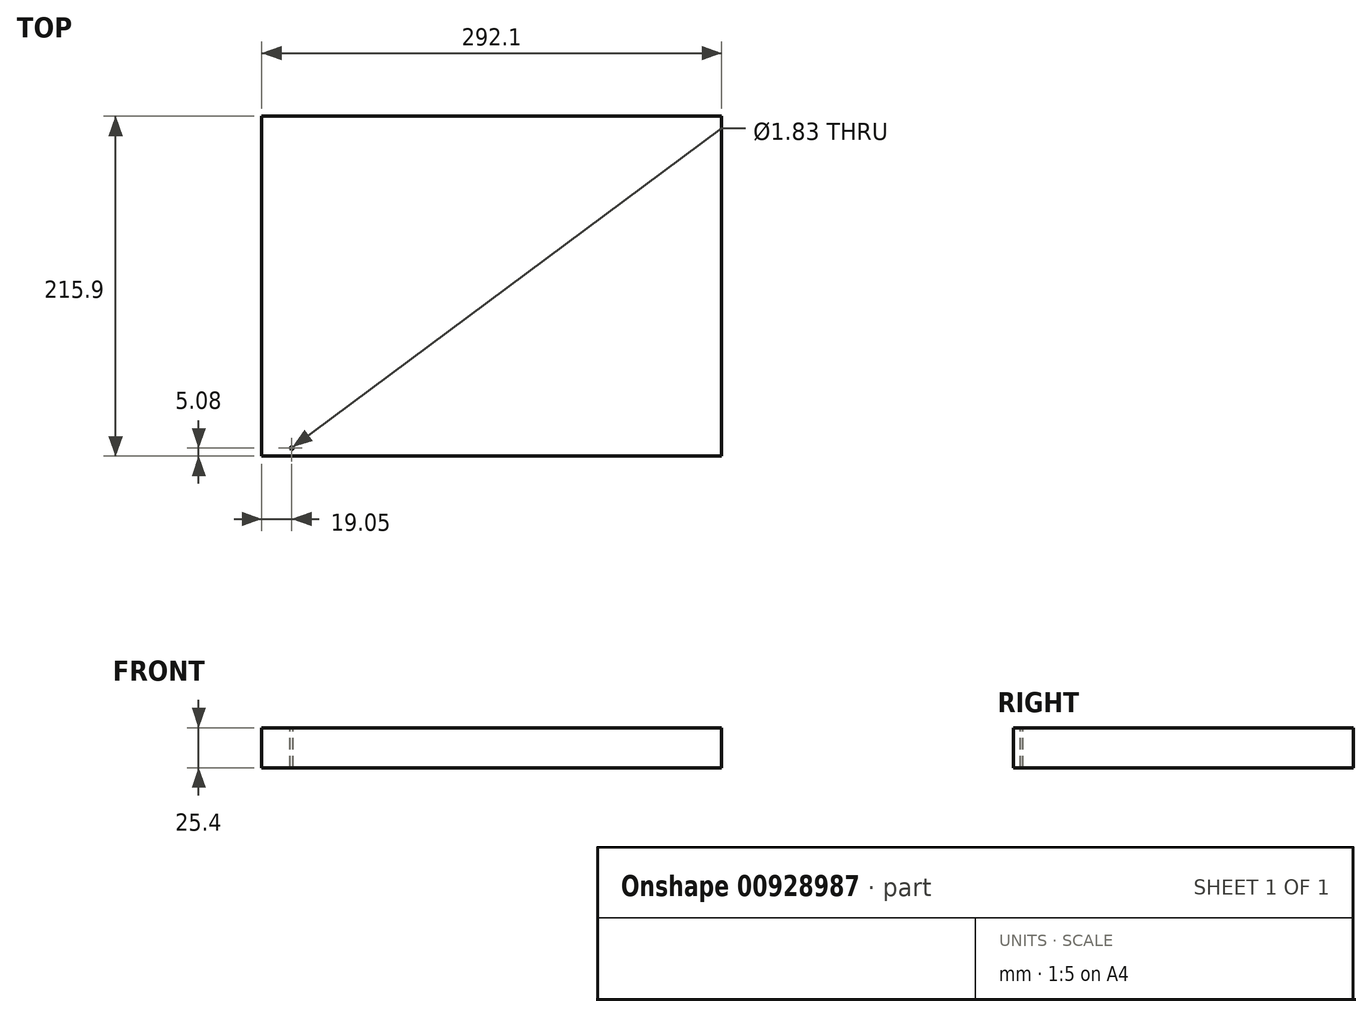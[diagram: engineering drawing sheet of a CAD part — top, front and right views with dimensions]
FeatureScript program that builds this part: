
annotation { "Feature Type Name" : "Feature", "Feature Type Description" : "" }
export const myFeature = defineFeature(function(context is Context, id is Id, definition is map)
    precondition{}
    {
        {
            var Q0;
            Q0=qCreatedBy(makeId("Top.planeOp"),FACE);
            var sketch = newSketch(context, id + "F0", { "sketchPlane" : qUnion([Q0])});
            skLineSegment(sketch, "E0.bottom", {"start": v(146.05, 107.95) * mm, "end": v(-146.05, 107.95) * mm});
            skLineSegment(sketch, "E0.top", {"start": v(146.05, -107.95) * mm, "end": v(-146.05, -107.95) * mm});
            skLineSegment(sketch, "E0.left", {"start": v(146.05, 107.95) * mm, "end": v(146.05, -107.95) * mm});
            skLineSegment(sketch, "E0.right", {"start": v(-146.05, 107.95) * mm, "end": v(-146.05, -107.95) * mm});
            skPoint(sketch, "E0.middle", {"position": v(0, 0) * mm});
            skSolve(sketch);
        }
        {
            var Q0;
            Q0=makeQuery(id+"F0.imprint","IMPRINT",FACE,{"disambiguationData":[TD([[makeQuery(id+"F0.imprint","IMPRINT",EDGE,{"derivedFrom":sQuery(id+"F0.wireOp",EDGE,"E0.bottom")}),1.0]])]});
            extrude(context, id + "F1", {"entities" : qUnion([Q0]), "depth" : 25.4 * mm, "offsetDistance" : 25.4 * mm});
        }
        {
            var Q0;
            Q0=makeQuery(id+"F1.opExtrude","CAP_FACE",FACE,{"disambiguationData":[OSD([sQuery(id+"F0.wireOp",EDGE,"E0.bottom"),sQuery(id+"F0.wireOp",EDGE,"E0.top"),sQuery(id+"F0.wireOp",EDGE,"E0.left"),sQuery(id+"F0.wireOp",EDGE,"E0.right")])],"isStart":false});
            var sketch = newSketch(context, id + "F2", { "sketchPlane" : qUnion([Q0])});
            skCircle(sketch, "E1", {"center": v(-127, -102.87) * mm, "radius": 0.91 * mm});
            skCircle(sketch, "E2.1.0.0", {"center": v(-124.46, -102.87) * mm, "radius": 0.91 * mm});
            skCircle(sketch, "E2.2.0.0", {"center": v(-121.92, -102.87) * mm, "radius": 0.91 * mm});
            skCircle(sketch, "E2.3.0.0", {"center": v(-119.38, -102.87) * mm, "radius": 0.91 * mm});
            skCircle(sketch, "E2.4.0.0", {"center": v(-116.84, -102.87) * mm, "radius": 0.91 * mm});
            skCircle(sketch, "E2.5.0.0", {"center": v(-114.3, -102.87) * mm, "radius": 0.91 * mm});
            skCircle(sketch, "E2.6.0.0", {"center": v(-111.76, -102.87) * mm, "radius": 0.91 * mm});
            skCircle(sketch, "E2.7.0.0", {"center": v(-109.22, -102.87) * mm, "radius": 0.91 * mm});
            skCircle(sketch, "E2.8.0.0", {"center": v(-106.68, -102.87) * mm, "radius": 0.91 * mm});
            skCircle(sketch, "E2.9.0.0", {"center": v(-104.14, -102.87) * mm, "radius": 0.91 * mm});
            skCircle(sketch, "E2.10.0.0", {"center": v(-101.6, -102.87) * mm, "radius": 0.91 * mm});
            skCircle(sketch, "E2.11.0.0", {"center": v(-99.06, -102.87) * mm, "radius": 0.91 * mm});
            skCircle(sketch, "E2.12.0.0", {"center": v(-96.52, -102.87) * mm, "radius": 0.91 * mm});
            skCircle(sketch, "E2.13.0.0", {"center": v(-93.98, -102.87) * mm, "radius": 0.91 * mm});
            skCircle(sketch, "E2.14.0.0", {"center": v(-91.44, -102.87) * mm, "radius": 0.91 * mm});
            skCircle(sketch, "E2.15.0.0", {"center": v(-88.9, -102.87) * mm, "radius": 0.91 * mm});
            skCircle(sketch, "E2.16.0.0", {"center": v(-86.36, -102.87) * mm, "radius": 0.91 * mm});
            skCircle(sketch, "E2.17.0.0", {"center": v(-83.82, -102.87) * mm, "radius": 0.91 * mm});
            skCircle(sketch, "E2.18.0.0", {"center": v(-81.28, -102.87) * mm, "radius": 0.91 * mm});
            skCircle(sketch, "E2.19.0.0", {"center": v(-78.74, -102.87) * mm, "radius": 0.91 * mm});
            skCircle(sketch, "E2.20.0.0", {"center": v(-76.2, -102.87) * mm, "radius": 0.91 * mm});
            skCircle(sketch, "E2.21.0.0", {"center": v(-73.66, -102.87) * mm, "radius": 0.91 * mm});
            skCircle(sketch, "E2.22.0.0", {"center": v(-71.12, -102.87) * mm, "radius": 0.91 * mm});
            skCircle(sketch, "E2.23.0.0", {"center": v(-68.58, -102.87) * mm, "radius": 0.91 * mm});
            skCircle(sketch, "E2.24.0.0", {"center": v(-66.04, -102.87) * mm, "radius": 0.91 * mm});
            skCircle(sketch, "E2.25.0.0", {"center": v(-63.5, -102.87) * mm, "radius": 0.91 * mm});
            skCircle(sketch, "E2.26.0.0", {"center": v(-60.96, -102.87) * mm, "radius": 0.91 * mm});
            skCircle(sketch, "E2.27.0.0", {"center": v(-58.42, -102.87) * mm, "radius": 0.91 * mm});
            skCircle(sketch, "E2.28.0.0", {"center": v(-55.88, -102.87) * mm, "radius": 0.91 * mm});
            skCircle(sketch, "E2.29.0.0", {"center": v(-53.34, -102.87) * mm, "radius": 0.91 * mm});
            skCircle(sketch, "E2.30.0.0", {"center": v(-50.8, -102.87) * mm, "radius": 0.91 * mm});
            skCircle(sketch, "E2.31.0.0", {"center": v(-48.26, -102.87) * mm, "radius": 0.91 * mm});
            skCircle(sketch, "E2.32.0.0", {"center": v(-45.72, -102.87) * mm, "radius": 0.91 * mm});
            skCircle(sketch, "E2.33.0.0", {"center": v(-43.18, -102.87) * mm, "radius": 0.91 * mm});
            skCircle(sketch, "E2.34.0.0", {"center": v(-40.64, -102.87) * mm, "radius": 0.91 * mm});
            skCircle(sketch, "E2.35.0.0", {"center": v(-38.1, -102.87) * mm, "radius": 0.91 * mm});
            skCircle(sketch, "E2.36.0.0", {"center": v(-35.56, -102.87) * mm, "radius": 0.91 * mm});
            skCircle(sketch, "E2.37.0.0", {"center": v(-33.02, -102.87) * mm, "radius": 0.91 * mm});
            skCircle(sketch, "E2.38.0.0", {"center": v(-30.48, -102.87) * mm, "radius": 0.91 * mm});
            skCircle(sketch, "E2.39.0.0", {"center": v(-27.94, -102.87) * mm, "radius": 0.91 * mm});
            skCircle(sketch, "E2.40.0.0", {"center": v(-25.4, -102.87) * mm, "radius": 0.91 * mm});
            skCircle(sketch, "E2.41.0.0", {"center": v(-22.86, -102.87) * mm, "radius": 0.91 * mm});
            skCircle(sketch, "E2.42.0.0", {"center": v(-20.32, -102.87) * mm, "radius": 0.91 * mm});
            skCircle(sketch, "E2.43.0.0", {"center": v(-17.78, -102.87) * mm, "radius": 0.91 * mm});
            skCircle(sketch, "E2.44.0.0", {"center": v(-15.24, -102.87) * mm, "radius": 0.91 * mm});
            skCircle(sketch, "E2.45.0.0", {"center": v(-12.7, -102.87) * mm, "radius": 0.91 * mm});
            skCircle(sketch, "E2.46.0.0", {"center": v(-10.16, -102.87) * mm, "radius": 0.91 * mm});
            skCircle(sketch, "E2.47.0.0", {"center": v(-7.62, -102.87) * mm, "radius": 0.91 * mm});
            skCircle(sketch, "E2.48.0.0", {"center": v(-5.08, -102.87) * mm, "radius": 0.91 * mm});
            skCircle(sketch, "E2.49.0.0", {"center": v(-2.54, -102.87) * mm, "radius": 0.91 * mm});
            skCircle(sketch, "E2.50.0.0", {"center": v(0, -102.87) * mm, "radius": 0.91 * mm});
            skCircle(sketch, "E2.51.0.0", {"center": v(2.54, -102.87) * mm, "radius": 0.91 * mm});
            skCircle(sketch, "E2.52.0.0", {"center": v(5.08, -102.87) * mm, "radius": 0.91 * mm});
            skCircle(sketch, "E2.53.0.0", {"center": v(7.62, -102.87) * mm, "radius": 0.91 * mm});
            skCircle(sketch, "E2.54.0.0", {"center": v(10.16, -102.87) * mm, "radius": 0.91 * mm});
            skCircle(sketch, "E2.55.0.0", {"center": v(12.7, -102.87) * mm, "radius": 0.91 * mm});
            skCircle(sketch, "E2.56.0.0", {"center": v(15.24, -102.87) * mm, "radius": 0.91 * mm});
            skCircle(sketch, "E2.57.0.0", {"center": v(17.78, -102.87) * mm, "radius": 0.91 * mm});
            skCircle(sketch, "E2.58.0.0", {"center": v(20.32, -102.87) * mm, "radius": 0.91 * mm});
            skCircle(sketch, "E2.59.0.0", {"center": v(22.86, -102.87) * mm, "radius": 0.91 * mm});
            skCircle(sketch, "E2.60.0.0", {"center": v(25.4, -102.87) * mm, "radius": 0.91 * mm});
            skCircle(sketch, "E2.61.0.0", {"center": v(27.94, -102.87) * mm, "radius": 0.91 * mm});
            skCircle(sketch, "E2.62.0.0", {"center": v(30.48, -102.87) * mm, "radius": 0.91 * mm});
            skCircle(sketch, "E2.63.0.0", {"center": v(33.02, -102.87) * mm, "radius": 0.91 * mm});
            skCircle(sketch, "E2.64.0.0", {"center": v(35.56, -102.87) * mm, "radius": 0.91 * mm});
            skCircle(sketch, "E2.65.0.0", {"center": v(38.1, -102.87) * mm, "radius": 0.91 * mm});
            skCircle(sketch, "E2.66.0.0", {"center": v(40.64, -102.87) * mm, "radius": 0.91 * mm});
            skCircle(sketch, "E2.67.0.0", {"center": v(43.18, -102.87) * mm, "radius": 0.91 * mm});
            skCircle(sketch, "E2.68.0.0", {"center": v(45.72, -102.87) * mm, "radius": 0.91 * mm});
            skCircle(sketch, "E2.69.0.0", {"center": v(48.26, -102.87) * mm, "radius": 0.91 * mm});
            skCircle(sketch, "E2.70.0.0", {"center": v(50.8, -102.87) * mm, "radius": 0.91 * mm});
            skCircle(sketch, "E2.71.0.0", {"center": v(53.34, -102.87) * mm, "radius": 0.91 * mm});
            skCircle(sketch, "E2.72.0.0", {"center": v(55.88, -102.87) * mm, "radius": 0.91 * mm});
            skCircle(sketch, "E2.73.0.0", {"center": v(58.42, -102.87) * mm, "radius": 0.91 * mm});
            skCircle(sketch, "E2.74.0.0", {"center": v(60.96, -102.87) * mm, "radius": 0.91 * mm});
            skCircle(sketch, "E2.75.0.0", {"center": v(63.5, -102.87) * mm, "radius": 0.91 * mm});
            skCircle(sketch, "E2.76.0.0", {"center": v(66.04, -102.87) * mm, "radius": 0.91 * mm});
            skCircle(sketch, "E2.77.0.0", {"center": v(68.58, -102.87) * mm, "radius": 0.91 * mm});
            skCircle(sketch, "E2.78.0.0", {"center": v(71.12, -102.87) * mm, "radius": 0.91 * mm});
            skCircle(sketch, "E2.79.0.0", {"center": v(73.66, -102.87) * mm, "radius": 0.91 * mm});
            skCircle(sketch, "E2.80.0.0", {"center": v(76.2, -102.87) * mm, "radius": 0.91 * mm});
            skCircle(sketch, "E2.81.0.0", {"center": v(78.74, -102.87) * mm, "radius": 0.91 * mm});
            skCircle(sketch, "E2.82.0.0", {"center": v(81.28, -102.87) * mm, "radius": 0.91 * mm});
            skCircle(sketch, "E2.83.0.0", {"center": v(83.82, -102.87) * mm, "radius": 0.91 * mm});
            skCircle(sketch, "E2.84.0.0", {"center": v(86.36, -102.87) * mm, "radius": 0.91 * mm});
            skCircle(sketch, "E2.85.0.0", {"center": v(88.9, -102.87) * mm, "radius": 0.91 * mm});
            skCircle(sketch, "E2.86.0.0", {"center": v(91.44, -102.87) * mm, "radius": 0.91 * mm});
            skCircle(sketch, "E2.87.0.0", {"center": v(93.98, -102.87) * mm, "radius": 0.91 * mm});
            skCircle(sketch, "E2.88.0.0", {"center": v(96.52, -102.87) * mm, "radius": 0.91 * mm});
            skCircle(sketch, "E2.89.0.0", {"center": v(99.06, -102.87) * mm, "radius": 0.91 * mm});
            skCircle(sketch, "E2.90.0.0", {"center": v(101.6, -102.87) * mm, "radius": 0.91 * mm});
            skCircle(sketch, "E2.91.0.0", {"center": v(104.14, -102.87) * mm, "radius": 0.91 * mm});
            skCircle(sketch, "E2.92.0.0", {"center": v(106.68, -102.87) * mm, "radius": 0.91 * mm});
            skCircle(sketch, "E2.93.0.0", {"center": v(109.22, -102.87) * mm, "radius": 0.91 * mm});
            skCircle(sketch, "E2.94.0.0", {"center": v(111.76, -102.87) * mm, "radius": 0.91 * mm});
            skCircle(sketch, "E2.95.0.0", {"center": v(114.3, -102.87) * mm, "radius": 0.91 * mm});
            skCircle(sketch, "E2.96.0.0", {"center": v(116.84, -102.87) * mm, "radius": 0.91 * mm});
            skCircle(sketch, "E2.97.0.0", {"center": v(119.38, -102.87) * mm, "radius": 0.91 * mm});
            skCircle(sketch, "E2.98.0.0", {"center": v(121.92, -102.87) * mm, "radius": 0.91 * mm});
            skCircle(sketch, "E2.99.0.0", {"center": v(124.46, -102.87) * mm, "radius": 0.91 * mm});
            skLineSegment(sketch, "E2.direction1", {"start": v(-127, -102.87) * mm, "end": v(-124.46, -102.87) * mm, "construction": true});
            skSolve(sketch);
        }
        {
            var Q0;
            Q0=sQuery(id+"F2.wireOp",VERTEX,"E1.center");
            var Q1;
            Q1=makeQuery(id+"F1.opExtrude","SWEPT_BODY",BODY,{"disambiguationData":[OSD([sQuery(id+"F0.wireOp",EDGE,"E0.bottom"),sQuery(id+"F0.wireOp",EDGE,"E0.top"),sQuery(id+"F0.wireOp",EDGE,"E0.left"),sQuery(id+"F0.wireOp",EDGE,"E0.right")])]});
            hole(context, id + "F3", {"style" : HoleStyle.SIMPLE, "endStyle" : HoleEndStyle.THROUGH, "holeDiameter" : 1.83 * mm, "majorDiameter" : 6.35 * mm, "isTappedThrough" : true, "tappedDepth" : 12.7 * mm, "tapClearance" : 3, "locations" : qUnion([Q0]), "scope" : qUnion([Q1])});
        }
    });
